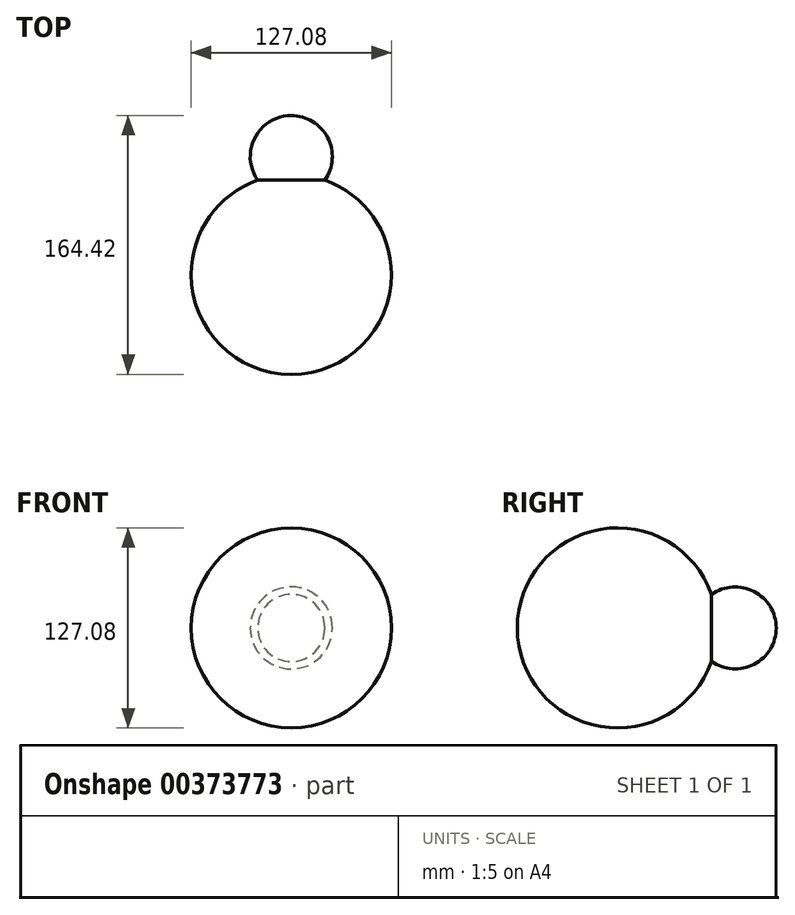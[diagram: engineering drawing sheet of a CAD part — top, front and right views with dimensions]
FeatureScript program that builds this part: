
annotation { "Feature Type Name" : "Feature", "Feature Type Description" : "" }
export const myFeature = defineFeature(function(context is Context, id is Id, definition is map)
    precondition{}
    {
        {
            var Q0;
            Q0=qCreatedBy(makeId("Top.planeOp"),FACE);
            var sketch = newSketch(context, id + "F0", { "sketchPlane" : qUnion([Q0])});
            skArc(sketch, "E0", {"start": v(63.54, 0) * mm, "mid": v(0, 63.54) * mm, "end": v(-63.54, 0) * mm});
            skLineSegment(sketch, "E1", {"start": v(-63.54, 0) * mm, "end": v(63.54, 0) * mm});
            skSolve(sketch);
        }
        {
            var Q0;
            Q0=makeQuery(id+"F0.imprint","IMPRINT",FACE,{"disambiguationData":[TD([[makeQuery(id+"F0.imprint","IMPRINT",EDGE,{"derivedFrom":sQuery(id+"F0.wireOp",EDGE,"E0")}),1.0]])]});
            var Q1;
            Q1=sQuery(id+"F0.wireOp",EDGE,"E1");
            revolve(context, id + "F1", {"entities" : qUnion([Q0]), "axis" : qUnion([Q1]), "revolveType" : RevolveType.FULL});
        }
        {
            var Q0;
            Q0=qCreatedBy(makeId("Top.planeOp"),FACE);
            var sketch = newSketch(context, id + "F2", { "sketchPlane" : qUnion([Q0])});
            skArc(sketch, "E2", {"start": v(0, 74.87) * mm, "mid": v(-8.1, 69.4) * mm, "end": v(0, 63.92) * mm});
            skLineSegment(sketch, "E3", {"start": v(0, 74.87) * mm, "end": v(0, 63.92) * mm});
            skSolve(sketch);
        }
        {
            var Q0;
            Q0=makeQuery(id+"F2.imprint","IMPRINT",FACE,{"disambiguationData":[TD([[makeQuery(id+"F2.imprint","IMPRINT",EDGE,{"derivedFrom":sQuery(id+"F2.wireOp",EDGE,"E2")}),1.0]])]});
            var Q1;
            Q1=sQuery(id+"F2.wireOp",EDGE,"E3");
            revolve(context, id + "F3", {"operationType" : NewBodyOperationType.ADD, "entities" : qUnion([Q0]), "axis" : qUnion([Q1]), "revolveType" : RevolveType.FULL});
        }
        {
            var Q0;
            Q0=qCreatedBy(makeId("Top.planeOp"),FACE);
            var sketch = newSketch(context, id + "F4", { "sketchPlane" : qUnion([Q0])});
            skArc(sketch, "E4", {"start": v(0, 100.88) * mm, "mid": v(26.07, 74.8) * mm, "end": v(0, 48.74) * mm});
            skLineSegment(sketch, "E5", {"start": v(0, 100.88) * mm, "end": v(0, 48.74) * mm});
            skSolve(sketch);
        }
        {
            var Q0;
            Q0 = qSketchRegion(id + "F4", true);
            var Q1;
            Q1=sQuery(id+"F4.wireOp",EDGE,"E5");
            revolve(context, id + "F5", {"operationType" : NewBodyOperationType.ADD, "entities" : qUnion([Q0]), "axis" : qUnion([Q1]), "revolveType" : RevolveType.FULL});
        }
    });
